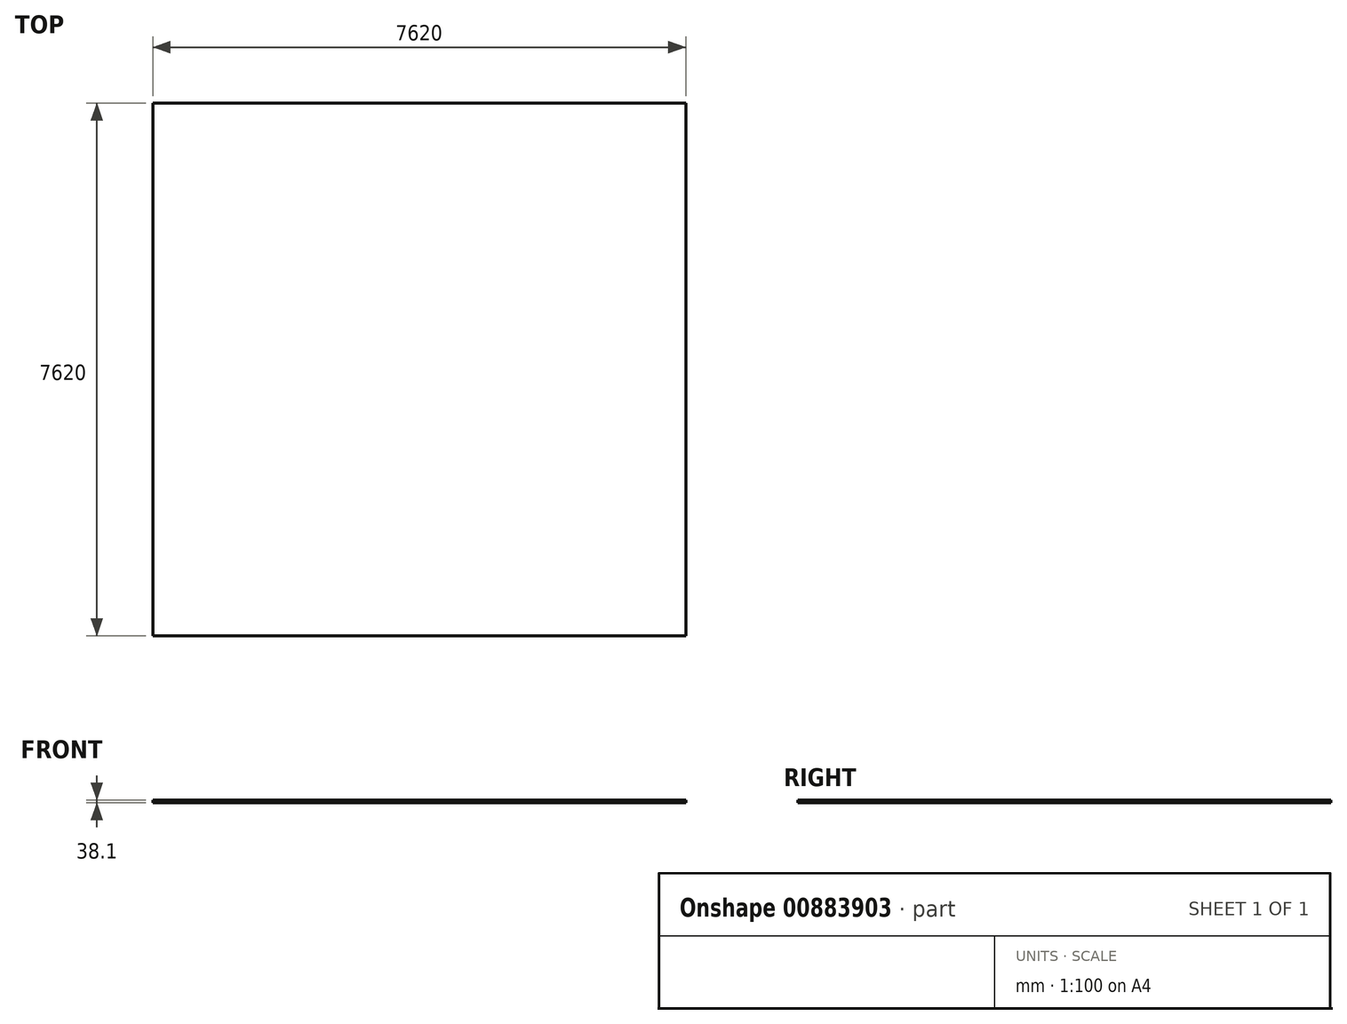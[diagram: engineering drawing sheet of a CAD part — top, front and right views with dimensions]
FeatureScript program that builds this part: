
annotation { "Feature Type Name" : "Feature", "Feature Type Description" : "" }
export const myFeature = defineFeature(function(context is Context, id is Id, definition is map)
    precondition{}
    {
        {
            var Q0;
            Q0=qCreatedBy(makeId("Top.planeOp"),FACE);
            cPlane(context, id + "F0", {"entities" : qUnion([Q0]), "cplaneType" : CPlaneType.OFFSET, "offset" : 2438.4 * mm, "width" : 152.4 * mm, "height" : 152.4 * mm});
        }
        {
            var Q0;
            Q0=qCreatedBy(makeId("Top.planeOp"),FACE);
            var sketch = newSketch(context, id + "F1", { "sketchPlane" : qUnion([Q0])});
            skLineSegment(sketch, "E0.bottom", {"start": v(3810, -3810) * mm, "end": v(-3810, -3810) * mm});
            skLineSegment(sketch, "E0.top", {"start": v(3810, 3810) * mm, "end": v(-3810, 3810) * mm});
            skLineSegment(sketch, "E0.left", {"start": v(3810, -3810) * mm, "end": v(3810, 3810) * mm});
            skLineSegment(sketch, "E0.right", {"start": v(-3810, -3810) * mm, "end": v(-3810, 3810) * mm});
            skPoint(sketch, "E0.middle", {"position": v(0, 0) * mm});
            skLineSegment(sketch, "E1.bottom", {"start": v(-3860.8, -3860.8) * mm, "end": v(3860.8, -3860.8) * mm});
            skLineSegment(sketch, "E1.top", {"start": v(-3860.8, 3860.8) * mm, "end": v(3860.8, 3860.8) * mm});
            skLineSegment(sketch, "E1.left", {"start": v(-3860.8, -3860.8) * mm, "end": v(-3860.8, 3860.8) * mm});
            skLineSegment(sketch, "E1.right", {"start": v(3860.8, -3860.8) * mm, "end": v(3860.8, 3860.8) * mm});
            skSolve(sketch);
        }
        {
            var Q0;
            Q0=sQuery(id+"F1.wireOp",EDGE,"E1.left");
            var Q1;
            Q1=sQuery(id+"F1.wireOp",VERTEX,"E1.bottom.start");
            cPlane(context, id + "F2", {"entities" : qUnion([Q0, Q1]), "cplaneType" : CPlaneType.LINE_POINT, "offset" : 25.4 * mm, "width" : 152.4 * mm, "height" : 152.4 * mm});
        }
        {
            var Q0;
            Q0=qCreatedBy(id+"F2.planeOp",FACE);
            var sketch = newSketch(context, id + "F3", { "sketchPlane" : qUnion([Q0])});
            skLineSegment(sketch, "E2", {"start": v(3860.8, 0) * mm, "end": v(3860.8, 2438.4) * mm});
            skLineSegment(sketch, "E3", {"start": v(-3860.8, 0) * mm, "end": v(-3860.8, 2438.4) * mm});
            skLineSegment(sketch, "E4", {"start": v(2641.6, 0) * mm, "end": v(2641.6, 2438.4) * mm});
            skLineSegment(sketch, "E5", {"start": v(-2641.6, 0) * mm, "end": v(-2641.6, 2438.4) * mm});
            skSolve(sketch);
        }
        {
            var Q0;
            Q0=sQuery(id+"F1.wireOp",EDGE,"E1.right");
            var Q1;
            Q1=sQuery(id+"F1.wireOp",VERTEX,"E1.top.end");
            cPlane(context, id + "F4", {"entities" : qUnion([Q0, Q1]), "cplaneType" : CPlaneType.LINE_POINT, "offset" : 25.4 * mm, "width" : 152.4 * mm, "height" : 152.4 * mm});
        }
        {
            var Q0;
            Q0=qCreatedBy(id+"F4.planeOp",FACE);
            var sketch = newSketch(context, id + "F5", { "sketchPlane" : qUnion([Q0])});
            skLineSegment(sketch, "E6", {"start": v(-3860.8, 0) * mm, "end": v(-3860.8, 2438.4) * mm});
            skLineSegment(sketch, "E7", {"start": v(3860.8, 0) * mm, "end": v(3860.8, 2438.4) * mm});
            skLineSegment(sketch, "E8", {"start": v(-3860.8, 2438.4) * mm, "end": v(3860.8, 2438.4) * mm});
            skSolve(sketch);
        }
        {
            var Q0;
            Q0=sQuery(id+"F5.wireOp",VERTEX,"E7.end");
            var Q1;
            Q1=sQuery(id+"F1.wireOp",VERTEX,"E1.top.start");
            var Q2;
            Q2=sQuery(id+"F3.wireOp",VERTEX,"E2.end");
            cPlane(context, id + "F6", {"entities" : qUnion([Q0, Q1, Q2]), "cplaneType" : CPlaneType.THREE_POINT, "offset" : 25.4 * mm, "width" : 152.4 * mm, "height" : 152.4 * mm});
        }
        {
            var Q0;
            Q0=qCreatedBy(id+"F6.planeOp",FACE);
            var sketch = newSketch(context, id + "F7", { "sketchPlane" : qUnion([Q0])});
            skLineSegment(sketch, "E9", {"start": v(3860.8, 2438.4) * mm, "end": v(-3860.8, 2438.4) * mm});
            skLineSegment(sketch, "E10", {"start": v(-2641.6, 0) * mm, "end": v(-2641.6, 2438.4) * mm});
            skSolve(sketch);
        }
        {
            var Q0;
            Q0=sQuery(id+"F3.wireOp",VERTEX,"E3.end");
            var Q1;
            Q1=sQuery(id+"F1.wireOp",VERTEX,"E1.bottom.end");
            var Q2;
            Q2=sQuery(id+"F5.wireOp",VERTEX,"E6.end");
            cPlane(context, id + "F8", {"entities" : qUnion([Q0, Q1, Q2]), "cplaneType" : CPlaneType.THREE_POINT, "offset" : 25.4 * mm, "width" : 152.4 * mm, "height" : 152.4 * mm});
        }
        {
            var Q0;
            Q0=qCreatedBy(id+"F8.planeOp",FACE);
            var sketch = newSketch(context, id + "F9", { "sketchPlane" : qUnion([Q0])});
            skLineSegment(sketch, "E11", {"start": v(-3860.8, 2438.4) * mm, "end": v(3860.8, 2438.4) * mm});
            skSolve(sketch);
        }
        {
            var Q0;
            Q0=sQuery(id+"F3.wireOp",VERTEX,"E2.end");
            var Q1;
            Q1=sQuery(id+"F1.wireOp",VERTEX,"E0.bottom.end");
            var Q2;
            Q2=sQuery(id+"F3.wireOp",VERTEX,"E3.end");
            cPlane(context, id + "F10", {"entities" : qUnion([Q0, Q1, Q2]), "cplaneType" : CPlaneType.THREE_POINT, "offset" : 25.4 * mm, "width" : 152.4 * mm, "height" : 152.4 * mm});
        }
        {
            var Q0;
            Q0=qCreatedBy(id+"F8.planeOp",FACE);
            var sketch = newSketch(context, id + "F11", { "sketchPlane" : qUnion([Q0])});
            skLineSegment(sketch, "E12", {"start": v(2641.6, 0) * mm, "end": v(2641.6, 2438.4) * mm});
            skSolve(sketch);
        }
        {
            var Q0;
            Q0=sQuery(id+"F3.wireOp",EDGE,"E2");
            var Q1;
            Q1=sQuery(id+"F3.wireOp",VERTEX,"E2.end");
            cPlane(context, id + "F12", {"entities" : qUnion([Q0, Q1]), "cplaneType" : CPlaneType.LINE_POINT, "offset" : 25.4 * mm, "width" : 152.4 * mm, "height" : 152.4 * mm});
        }
        {
            var Q0;
            Q0=makeQuery(id+"F1.imprint","IMPRINT",FACE,{"disambiguationData":[TD([[makeQuery(id+"F1.imprint","IMPRINT",EDGE,{"derivedFrom":sQuery(id+"F1.wireOp",EDGE,"E0.bottom")}),-1.0]])]});
            extrude(context, id + "F13", {"entities" : qUnion([Q0]), "oppositeDirection" : true, "depth" : 38.1 * mm, "offsetDistance" : 25.4 * mm});
        }
    });
